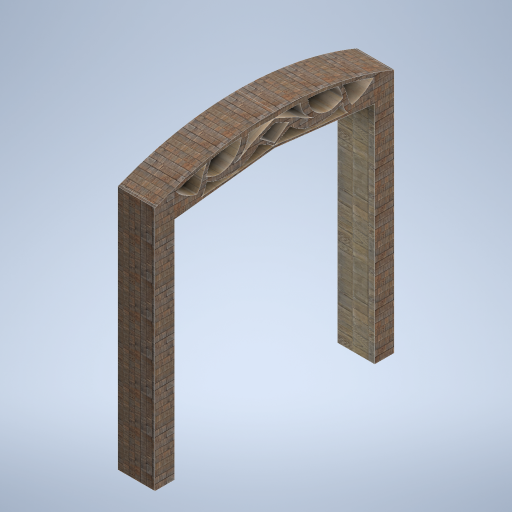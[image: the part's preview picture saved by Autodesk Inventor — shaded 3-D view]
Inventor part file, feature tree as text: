
AUTODESK INVENTOR PART (.ipt)
format: ipt  version: 2024.2 (Build 282272000, 272)  size: 474,624 bytes
history: native  units: mm
features: extrude x1, sketch x1
ambient origin geometry x8: Origin, YZ Plane, XZ Plane, XY Plane, X Axis, Y Axis, Z Axis, Center Point
bodies: Solid1 (feature_tree)
feature tree (2):
  extrude  "Extrusion1"  Depth=380.0mm
  sketch  "Sketch1"  dims[d0=200.0mm d1=2300.0mm d5=380.0mm d6=0.0mm]
